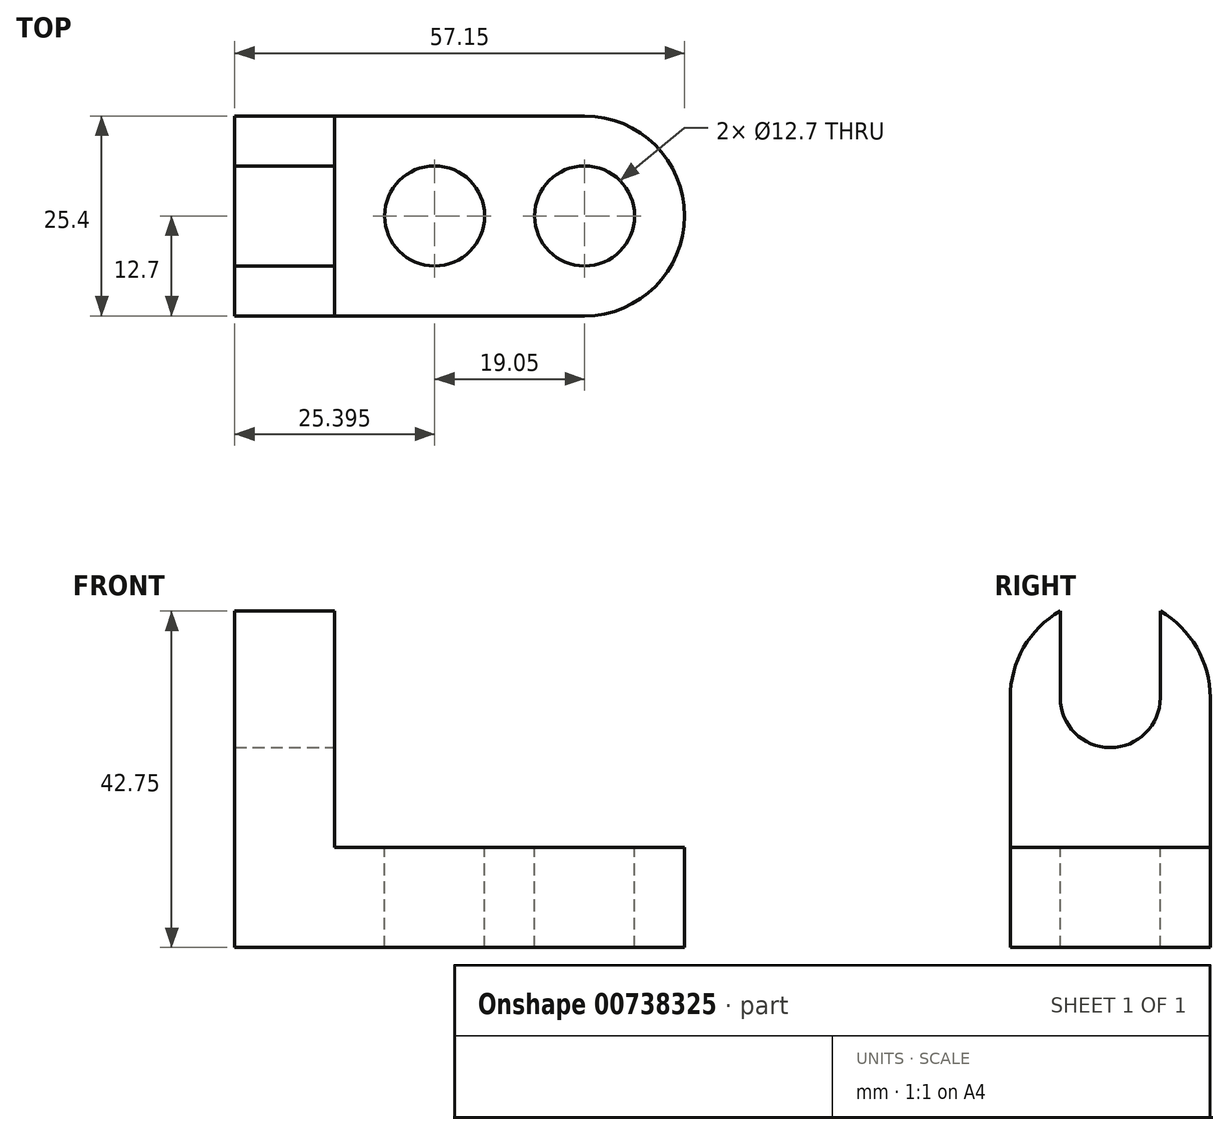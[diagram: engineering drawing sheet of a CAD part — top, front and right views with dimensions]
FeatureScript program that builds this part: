
annotation { "Feature Type Name" : "Feature", "Feature Type Description" : "" }
export const myFeature = defineFeature(function(context is Context, id is Id, definition is map)
    precondition{}
    {
        {
            var Q0;
            Q0=qCreatedBy(makeId("Front.planeOp"),FACE);
            var sketch = newSketch(context, id + "F0", { "sketchPlane" : qUnion([Q0])});
            skLineSegment(sketch, "E0", {"start": v(-34.65, 0) * mm, "end": v(-34.65, 44.45) * mm});
            skLineSegment(sketch, "E1", {"start": v(-34.65, 44.45) * mm, "end": v(-21.95, 44.45) * mm});
            skLineSegment(sketch, "E2", {"start": v(-21.95, 44.45) * mm, "end": v(-21.95, 12.7) * mm});
            skLineSegment(sketch, "E3", {"start": v(-21.95, 12.7) * mm, "end": v(22.5, 12.7) * mm});
            skLineSegment(sketch, "E4", {"start": v(22.5, 12.7) * mm, "end": v(22.5, 0) * mm});
            skLineSegment(sketch, "E5", {"start": v(22.5, 0) * mm, "end": v(-34.65, 0) * mm});
            skSolve(sketch);
        }
        {
            var Q0;
            Q0=makeQuery(id+"F0.imprint","IMPRINT",FACE,{"disambiguationData":[TD([[makeQuery(id+"F0.imprint","IMPRINT",EDGE,{"derivedFrom":sQuery(id+"F0.wireOp",EDGE,"E0")}),-1.0]])]});
            extrude(context, id + "F1", {"entities" : qUnion([Q0]), "depth" : 25.4 * mm, "offsetDistance" : 25.4 * mm});
        }
        {
            var Q0;
            Q0=makeQuery(id+"F1.opExtrude","SWEPT_FACE",FACE,{"disambiguationData":[OSD([sQuery(id+"F0.wireOp",EDGE,"E3")])]});
            var sketch = newSketch(context, id + "F2", { "sketchPlane" : qUnion([Q0])});
            skLineSegment(sketch, "E6", {"start": v(9.8, 0) * mm, "end": v(9.8, -25.4) * mm});
            skLineSegment(sketch, "E7", {"start": v(9.8, -25.4) * mm, "end": v(22.5, -25.4) * mm});
            skCircle(sketch, "E8", {"center": v(9.8, -12.7) * mm, "radius": 6.35 * mm});
            skLineSegment(sketch, "E9", {"start": v(-9.25, 0) * mm, "end": v(-9.25, -25.4) * mm});
            skLineSegment(sketch, "E10", {"start": v(-9.25, -25.4) * mm, "end": v(-21.95, -25.4) * mm});
            skCircle(sketch, "E11", {"center": v(-9.25, -12.7) * mm, "radius": 6.35 * mm});
            skArc(sketch, "E12", {"start": v(9.8, -25.4) * mm, "mid": v(22.5, -12.7) * mm, "end": v(9.8, 0) * mm});
            skSolve(sketch);
        }
        {
            var Q0;
            {var subQ0=sQuery(id+"F2.wireOp",EDGE,"E11");var subQ1=sQuery(id+"F2.wireOp",EDGE,"E9");var subQ2=makeQuery(id+"F2.imprint","INTERSECT",VERTEX,{"disambiguationData":[OD(0.0)],"derivedFrom":[subQ1,subQ0]});Q0=makeQuery(id+"F2.imprint","IMPRINT",FACE,{"disambiguationData":[TD([[makeQuery(id+"F2.imprint","IMPRINT",EDGE,{"disambiguationData":[TD([[subQ2,-1.0]])],"derivedFrom":subQ1}),1.0]])]});}
            var Q1;
            {var subQ0=sQuery(id+"F2.wireOp",EDGE,"E11");var subQ1=sQuery(id+"F2.wireOp",EDGE,"E9");var subQ2=makeQuery(id+"F2.imprint","INTERSECT",VERTEX,{"disambiguationData":[OD(0.0)],"derivedFrom":[subQ1,subQ0]});Q1=makeQuery(id+"F2.imprint","IMPRINT",FACE,{"disambiguationData":[TD([[makeQuery(id+"F2.imprint","IMPRINT",EDGE,{"disambiguationData":[TD([[subQ2,-1.0]])],"derivedFrom":subQ1}),-1.0]])]});}
            var Q2;
            {var subQ0=sQuery(id+"F2.wireOp",EDGE,"E8");var subQ1=sQuery(id+"F2.wireOp",EDGE,"E6");var subQ2=makeQuery(id+"F2.imprint","INTERSECT",VERTEX,{"disambiguationData":[OD(0.0)],"derivedFrom":[subQ1,subQ0]});Q2=makeQuery(id+"F2.imprint","IMPRINT",FACE,{"disambiguationData":[TD([[makeQuery(id+"F2.imprint","IMPRINT",EDGE,{"disambiguationData":[TD([[subQ2,-1.0]])],"derivedFrom":subQ1}),-1.0]])]});}
            var Q3;
            {var subQ0=sQuery(id+"F2.wireOp",EDGE,"E8");var subQ1=sQuery(id+"F2.wireOp",EDGE,"E6");var subQ2=makeQuery(id+"F2.imprint","INTERSECT",VERTEX,{"disambiguationData":[OD(0.0)],"derivedFrom":[subQ1,subQ0]});Q3=makeQuery(id+"F2.imprint","IMPRINT",FACE,{"disambiguationData":[TD([[makeQuery(id+"F2.imprint","IMPRINT",EDGE,{"disambiguationData":[TD([[subQ2,-1.0]])],"derivedFrom":subQ1}),1.0]])]});}
            var Q4;
            {var subQ0=sQuery(id+"F2.wireOp",EDGE,"E12");var subQ1=sQuery(id+"F0.wireOp",EDGE,"E3");var subQ2=makeQuery(id+"F1.opExtrude","CAP_EDGE",EDGE,{"disambiguationData":[OSD([subQ1])],"isStart":true});var subQ3=makeQuery(id+"F2.imprint","INTERSECT",VERTEX,{"derivedFrom":[subQ2,sQuery(id+"F2.wireOp",EDGE,"E6"),subQ0]});Q4=makeQuery(id+"F2.imprint","IMPRINT",FACE,{"disambiguationData":[TD([[makeQuery(id+"F2.imprint","IMPRINT",EDGE,{"disambiguationData":[TD([[subQ3,1.0]])],"derivedFrom":subQ0}),-1.0]])]});}
            var Q5;
            {var subQ0=sQuery(id+"F2.wireOp",EDGE,"E7");Q5=makeQuery(id+"F2.imprint","IMPRINT",FACE,{"disambiguationData":[TD([[makeQuery(id+"F2.imprint","IMPRINT",EDGE,{"derivedFrom":subQ0}),1.0]])]});}
            extrude(context, id + "F3", {"entities" : qUnion([Q0, Q1, Q2, Q3, Q4, Q5]), "operationType" : NewBodyOperationType.REMOVE, "endBound" : BoundingType.THROUGH_ALL, "oppositeDirection" : true, "depth" : 25.4 * mm, "offsetDistance" : 25.4 * mm});
        }
        {
            var Q0;
            Q0=makeQuery(id+"F1.opExtrude","SWEPT_FACE",FACE,{"disambiguationData":[OSD([sQuery(id+"F0.wireOp",EDGE,"E2")])]});
            var sketch = newSketch(context, id + "F4", { "sketchPlane" : qUnion([Q0])});
            skLineSegment(sketch, "E13", {"start": v(-25.4, 31.75) * mm, "end": v(0, 31.75) * mm});
            skLineSegment(sketch, "E14", {"start": v(-25.4, 31.75) * mm, "end": v(-25.4, 44.45) * mm});
            skCircle(sketch, "E15", {"center": v(-12.7, 31.75) * mm, "radius": 6.35 * mm});
            skArc(sketch, "E16", {"start": v(0, 31.75) * mm, "mid": v(-12.7, 44.45) * mm, "end": v(-25.4, 31.75) * mm});
            skLineSegment(sketch, "E17", {"start": v(-19.05, 31.75) * mm, "end": v(-19.05, 42.75) * mm});
            skLineSegment(sketch, "E18", {"start": v(-6.35, 31.75) * mm, "end": v(-6.35, 42.75) * mm});
            skSolve(sketch);
        }
        {
            var Q0;
            {var subQ0=sQuery(id+"F4.wireOp",EDGE,"E17");Q0=makeQuery(id+"F4.imprint","IMPRINT",FACE,{"disambiguationData":[TD([[makeQuery(id+"F4.imprint","IMPRINT",EDGE,{"derivedFrom":subQ0}),-1.0]])]});}
            var Q1;
            {var subQ0=sQuery(id+"F4.wireOp",EDGE,"E14");Q1=makeQuery(id+"F4.imprint","IMPRINT",FACE,{"disambiguationData":[TD([[makeQuery(id+"F4.imprint","IMPRINT",EDGE,{"derivedFrom":subQ0}),1.0]])]});}
            var Q2;
            {var subQ0=sQuery(id+"F4.wireOp",EDGE,"E16");var subQ4=makeQuery(id+"F4.imprint","INTERSECT",VERTEX,{"derivedFrom":[subQ0,sQuery(id+"F4.wireOp",EDGE,"E18")]});Q2=makeQuery(id+"F4.imprint","IMPRINT",FACE,{"disambiguationData":[TD([[makeQuery(id+"F4.imprint","IMPRINT",EDGE,{"disambiguationData":[TD([[subQ4,1.0]])],"derivedFrom":subQ0}),-1.0]])]});}
            var Q3;
            {var subQ0=sQuery(id+"F4.wireOp",EDGE,"E15");var subQ1=sQuery(id+"F4.wireOp",EDGE,"E13");var subQ2=makeQuery(id+"F4.imprint","INTERSECT",VERTEX,{"derivedFrom":[subQ1,subQ0,sQuery(id+"F4.wireOp",EDGE,"E17")]});Q3=makeQuery(id+"F4.imprint","IMPRINT",FACE,{"disambiguationData":[TD([[makeQuery(id+"F4.imprint","IMPRINT",EDGE,{"disambiguationData":[TD([[subQ2,-1.0]])],"derivedFrom":subQ1}),1.0]])]});}
            var Q4;
            {var subQ0=sQuery(id+"F4.wireOp",EDGE,"E15");var subQ1=sQuery(id+"F4.wireOp",EDGE,"E13");var subQ2=makeQuery(id+"F4.imprint","INTERSECT",VERTEX,{"derivedFrom":[subQ1,subQ0,sQuery(id+"F4.wireOp",EDGE,"E17")]});Q4=makeQuery(id+"F4.imprint","IMPRINT",FACE,{"disambiguationData":[TD([[makeQuery(id+"F4.imprint","IMPRINT",EDGE,{"disambiguationData":[TD([[subQ2,-1.0]])],"derivedFrom":subQ1}),-1.0]])]});}
            extrude(context, id + "F5", {"entities" : qUnion([Q0, Q1, Q2, Q3, Q4]), "operationType" : NewBodyOperationType.REMOVE, "endBound" : BoundingType.THROUGH_ALL, "oppositeDirection" : true, "depth" : 25.4 * mm, "offsetDistance" : 25.4 * mm});
        }
    });
